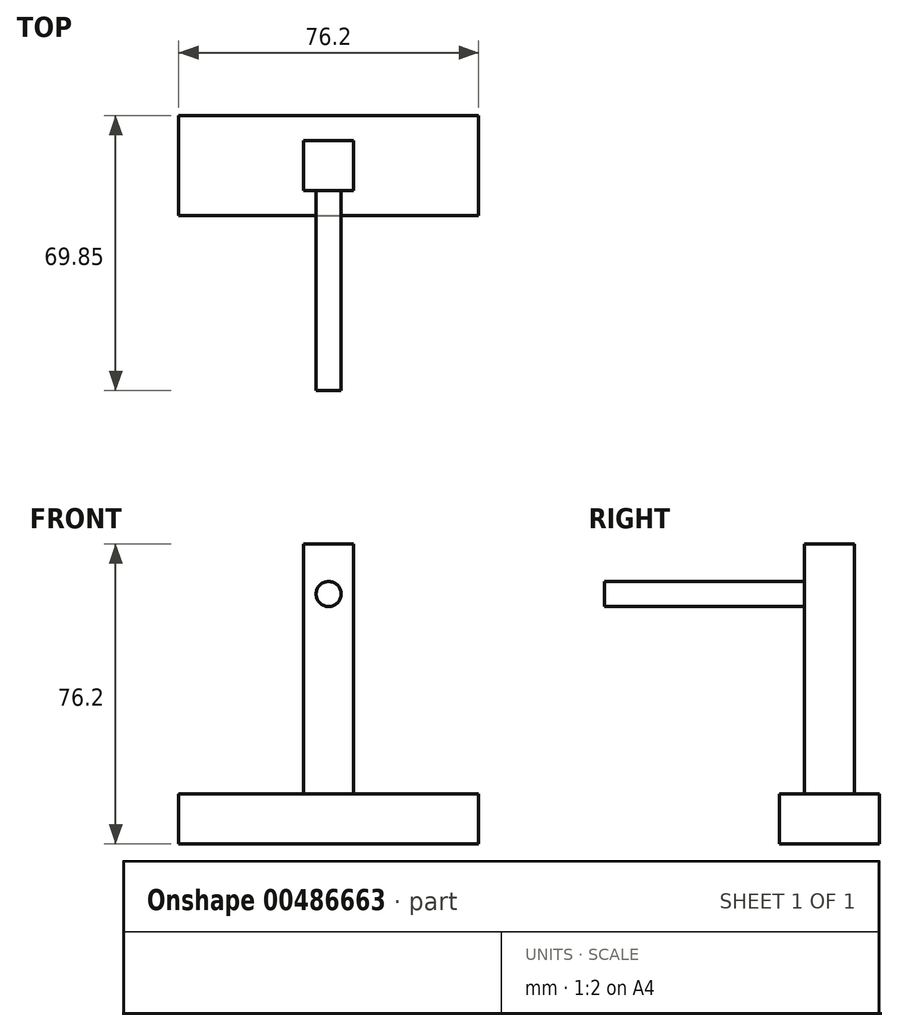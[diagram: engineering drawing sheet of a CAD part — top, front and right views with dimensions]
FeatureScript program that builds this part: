
annotation { "Feature Type Name" : "Feature", "Feature Type Description" : "" }
export const myFeature = defineFeature(function(context is Context, id is Id, definition is map)
    precondition{}
    {
        {
            var Q0;
            Q0=qCreatedBy(makeId("Top.planeOp"),FACE);
            var sketch = newSketch(context, id + "F0", { "sketchPlane" : qUnion([Q0])});
            skLineSegment(sketch, "E0.bottom", {"start": v(-38.1, 12.7) * mm, "end": v(38.1, 12.7) * mm});
            skLineSegment(sketch, "E0.top", {"start": v(-38.1, -12.7) * mm, "end": v(38.1, -12.7) * mm});
            skLineSegment(sketch, "E0.left", {"start": v(-38.1, 12.7) * mm, "end": v(-38.1, -12.7) * mm});
            skLineSegment(sketch, "E0.right", {"start": v(38.1, 12.7) * mm, "end": v(38.1, -12.7) * mm});
            skPoint(sketch, "E0.middle", {"position": v(0, 0) * mm});
            skSolve(sketch);
        }
        {
            var Q0;
            Q0=makeQuery(id+"F0.imprint","IMPRINT",FACE,{"disambiguationData":[TD([[makeQuery(id+"F0.imprint","IMPRINT",EDGE,{"derivedFrom":sQuery(id+"F0.wireOp",EDGE,"E0.bottom")}),-1.0]])]});
            extrude(context, id + "F1", {"entities" : qUnion([Q0]), "depth" : 12.7 * mm, "offsetDistance" : 25.4 * mm});
        }
        {
            var Q0;
            Q0=makeQuery(id+"F1.opExtrude","CAP_FACE",FACE,{"disambiguationData":[OSD([sQuery(id+"F0.wireOp",EDGE,"E0.bottom"),sQuery(id+"F0.wireOp",EDGE,"E0.top"),sQuery(id+"F0.wireOp",EDGE,"E0.left"),sQuery(id+"F0.wireOp",EDGE,"E0.right")])],"isStart":false});
            var sketch = newSketch(context, id + "F2", { "sketchPlane" : qUnion([Q0])});
            skLineSegment(sketch, "E1.bottom", {"start": v(-6.35, 6.35) * mm, "end": v(6.35, 6.35) * mm});
            skLineSegment(sketch, "E1.top", {"start": v(-6.35, -6.35) * mm, "end": v(6.35, -6.35) * mm});
            skLineSegment(sketch, "E1.left", {"start": v(-6.35, 6.35) * mm, "end": v(-6.35, -6.35) * mm});
            skLineSegment(sketch, "E1.right", {"start": v(6.35, 6.35) * mm, "end": v(6.35, -6.35) * mm});
            skPoint(sketch, "E1.middle", {"position": v(0, 0) * mm});
            skSolve(sketch);
        }
        {
            var Q0;
            Q0 = qSketchRegion(id + "F2", true);
            extrude(context, id + "F3", {"entities" : qUnion([Q0]), "operationType" : NewBodyOperationType.ADD, "depth" : 63.5 * mm, "offsetDistance" : 25.4 * mm});
        }
        {
            var Q0;
            Q0=makeQuery(id+"F3.opExtrude","SWEPT_FACE",FACE,{"disambiguationData":[OSD([sQuery(id+"F2.wireOp",EDGE,"E1.top")])]});
            var sketch = newSketch(context, id + "F4", { "sketchPlane" : qUnion([Q0])});
            skCircle(sketch, "E2", {"center": v(0, 63.5) * mm, "radius": 3.17 * mm});
            skSolve(sketch);
        }
        {
            var Q0;
            Q0 = qSketchRegion(id + "F4", true);
            extrude(context, id + "F5", {"entities" : qUnion([Q0]), "operationType" : NewBodyOperationType.ADD, "depth" : 50.8 * mm, "offsetDistance" : 25.4 * mm});
        }
    });
